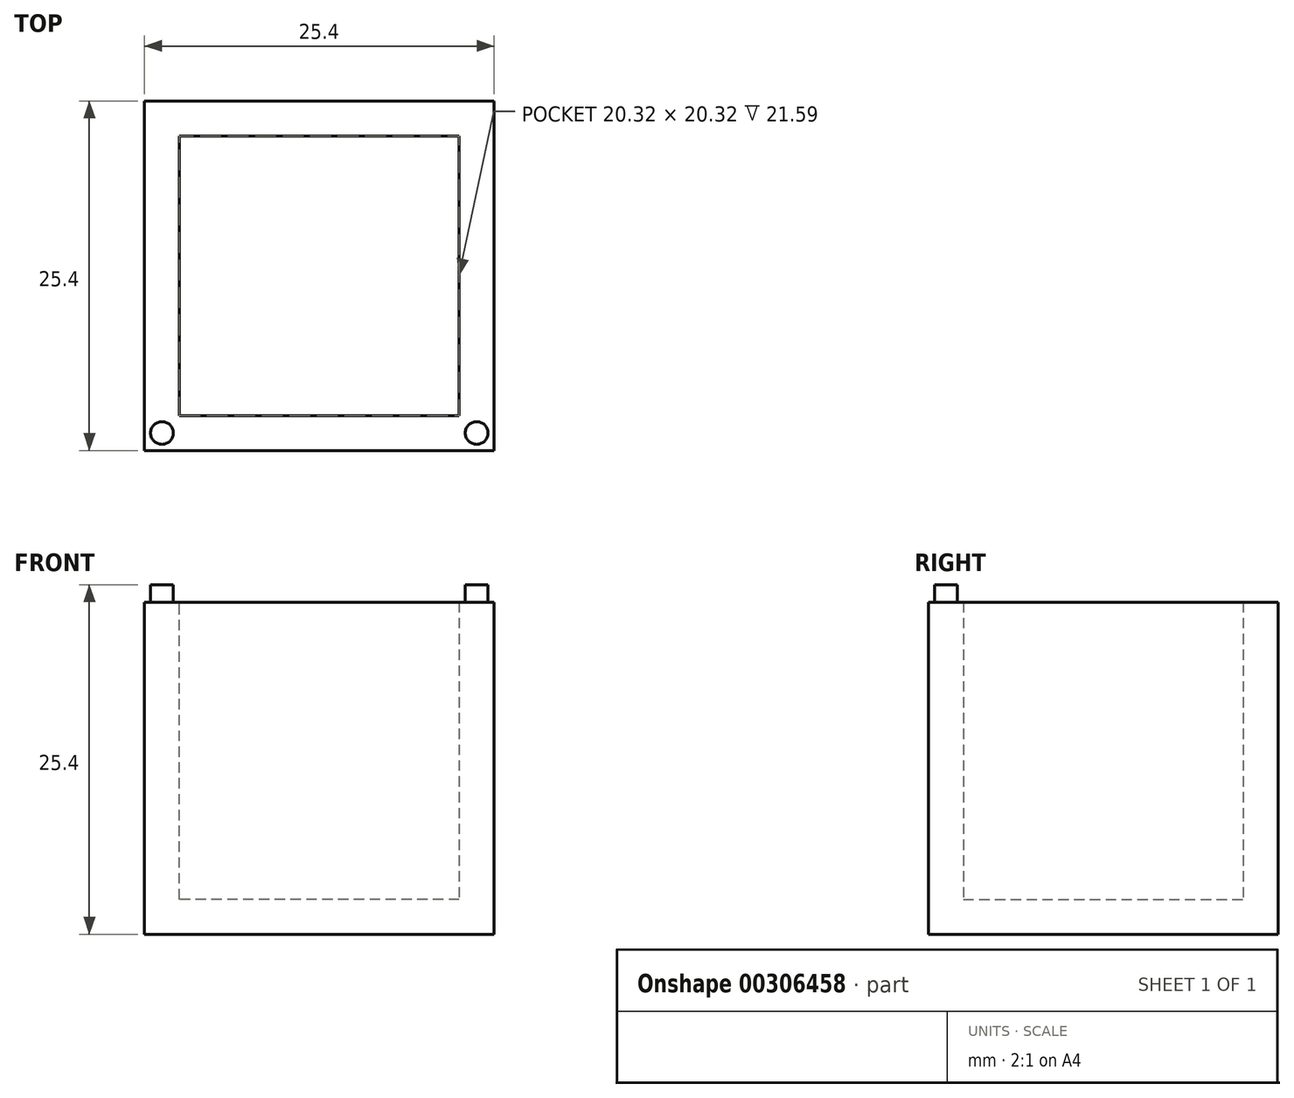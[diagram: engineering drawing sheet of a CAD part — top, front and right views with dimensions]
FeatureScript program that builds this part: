
annotation { "Feature Type Name" : "Feature", "Feature Type Description" : "" }
export const myFeature = defineFeature(function(context is Context, id is Id, definition is map)
    precondition{}
    {
        {
            var Q0;
            Q0=qCreatedBy(makeId("Front.planeOp"),FACE);
            var sketch = newSketch(context, id + "F0", { "sketchPlane" : qUnion([Q0])});
            skLineSegment(sketch, "E0", {"start": v(0, -12.7) * mm, "end": v(12.7, -12.7) * mm});
            skLineSegment(sketch, "E1", {"start": v(12.7, 0) * mm, "end": v(12.7, 12.7) * mm});
            skLineSegment(sketch, "E2", {"start": v(12.7, 0) * mm, "end": v(12.7, -12.7) * mm});
            skLineSegment(sketch, "E3", {"start": v(-12.7, 0) * mm, "end": v(-12.7, 12.7) * mm});
            skLineSegment(sketch, "E4", {"start": v(-12.7, 0) * mm, "end": v(-12.7, -12.7) * mm});
            skLineSegment(sketch, "E5", {"start": v(0, 12.7) * mm, "end": v(-12.7, 12.7) * mm});
            skLineSegment(sketch, "E6", {"start": v(0, -12.7) * mm, "end": v(-12.7, -12.7) * mm});
            skLineSegment(sketch, "E7", {"start": v(0, 12.7) * mm, "end": v(12.7, 12.7) * mm});
            skSolve(sketch);
        }
        {
            var Q0;
            Q0=makeQuery(id+"F0.imprint","IMPRINT",FACE,{"disambiguationData":[TD([[makeQuery(id+"F0.imprint","IMPRINT",EDGE,{"derivedFrom":sQuery(id+"F0.wireOp",EDGE,"E0")}),1.0]])]});
            extrude(context, id + "F1", {"entities" : qUnion([Q0]), "endBound" : BoundingType.SYMMETRIC, "depth" : 25.4 * mm});
        }
        {
            var Q0;
            Q0=makeQuery(id+"F1.opExtrude","SWEPT_FACE",FACE,{"disambiguationData":[OSD([sQuery(id+"F0.wireOp",EDGE,"E5"),sQuery(id+"F0.wireOp",EDGE,"E7")])]});
            shell(context, id + "F2", {"entities" : qUnion([Q0]), "thickness" : 2.54 * mm});
        }
        {
            var Q0;
            Q0=makeQuery(id+"F1.opExtrude","SWEPT_FACE",FACE,{"disambiguationData":[OSD([sQuery(id+"F0.wireOp",EDGE,"E5"),sQuery(id+"F0.wireOp",EDGE,"E7")])]});
            var sketch = newSketch(context, id + "F3", { "sketchPlane" : qUnion([Q0])});
            skCircle(sketch, "E8", {"center": v(-11.43, 11.43) * mm, "radius": 0.83 * mm});
            skCircle(sketch, "E9", {"center": v(11.43, 11.43) * mm, "radius": 0.83 * mm});
            skCircle(sketch, "E10.MirrorC", {"center": v(-11.43, -11.43) * mm, "radius": 0.83 * mm});
            skCircle(sketch, "E11.MirrorC", {"center": v(11.43, -11.43) * mm, "radius": 0.83 * mm});
            skSolve(sketch);
        }
        {
            var Q0;
            Q0=makeQuery(id+"F3.imprint","IMPRINT",FACE,{"disambiguationData":[TD([[makeQuery(id+"F3.imprint","IMPRINT",EDGE,{"derivedFrom":sQuery(id+"F3.wireOp",EDGE,"E8")}),1.0]])]});
            var Q1;
            Q1=makeQuery(id+"F3.imprint","IMPRINT",FACE,{"disambiguationData":[TD([[makeQuery(id+"F3.imprint","IMPRINT",EDGE,{"derivedFrom":sQuery(id+"F3.wireOp",EDGE,"E9")}),1.0]])]});
            var Q2;
            Q2=makeQuery(id+"F3.imprint","IMPRINT",FACE,{"disambiguationData":[TD([[makeQuery(id+"F3.imprint","IMPRINT",EDGE,{"derivedFrom":sQuery(id+"F3.wireOp",EDGE,"E11.MirrorC")}),-1.0]])]});
            var Q3;
            Q3=makeQuery(id+"F3.imprint","IMPRINT",FACE,{"disambiguationData":[TD([[makeQuery(id+"F3.imprint","IMPRINT",EDGE,{"derivedFrom":sQuery(id+"F3.wireOp",EDGE,"E10.MirrorC")}),-1.0]])]});
            extrude(context, id + "F4", {"entities" : qUnion([Q0, Q1, Q2, Q3]), "operationType" : NewBodyOperationType.REMOVE, "oppositeDirection" : true, "depth" : 1.27 * mm});
        }
    });
